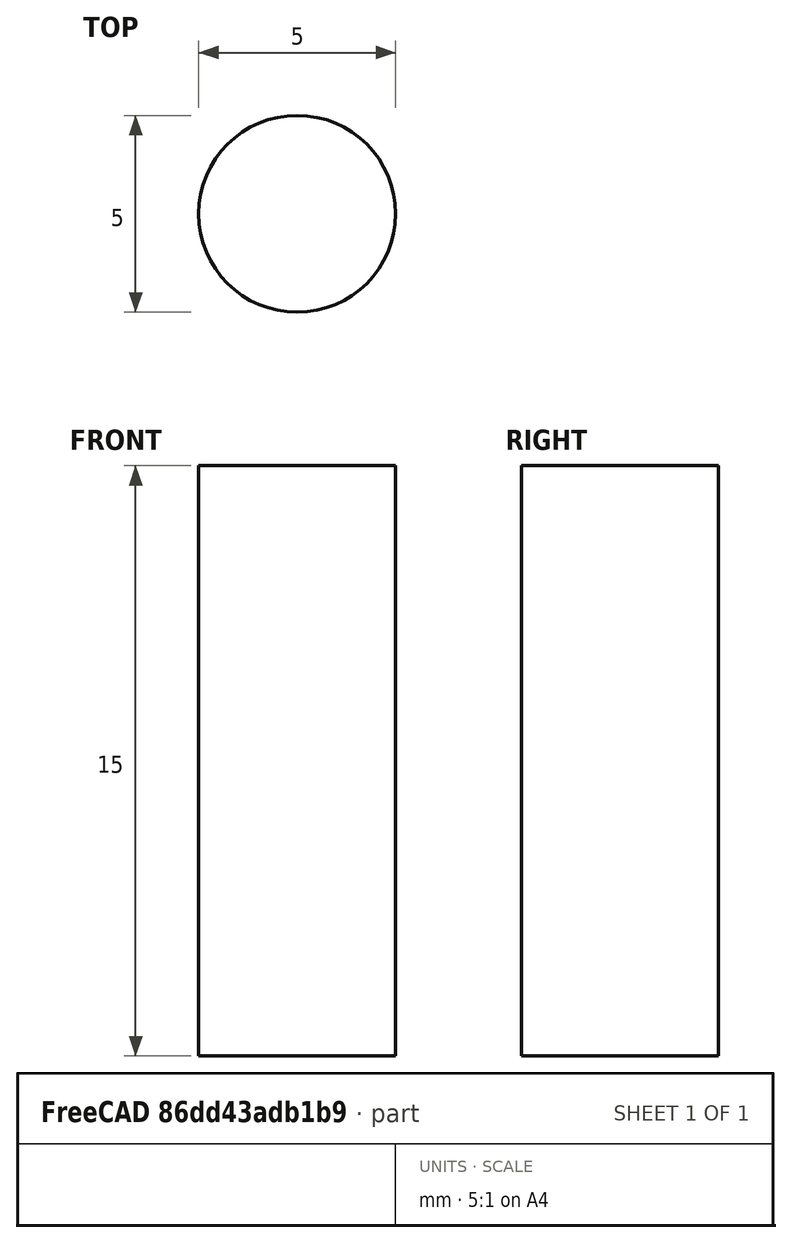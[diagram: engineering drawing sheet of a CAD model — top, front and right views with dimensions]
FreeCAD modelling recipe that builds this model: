
FCSTD DOCUMENT  (FreeCAD 1.0R39285 (Git))
Label: Box Pin
License: All rights reserved
LicenseURL: https://en.wikipedia.org/wiki/All_rights_reserved
objects: Sketcher::SketchObject×1, PartDesign::Pad×1, PartDesign::Body×1
note: 6 computed .brp shape members not serialized (recipe doc carries the construction recipe); baked Part::Feature solids carry a one-line shape summary decoded from their .brp

FEATURE [Sketcher::SketchObject] Sketch
  ArcFitTolerance = 1e-06
  AttachmentSupport = -> [XY_Plane]
  FullyConstrained = true
  MakeInternals = false
  MapMode = 5
  sketch-geometry (1):
    g0: Circle CenterX=0 CenterY=0 CenterZ=0 NormalX=0 NormalY=0 NormalZ=1 AngleXU=0 Radius=2.5
  constraints (2):
    c: Diameter(g0) = 5
    c: Coincident(g0,g-1)
FEATURE [PartDesign::Pad] Pad
  Direction = (0,0,1)
  Length = 15
  Length2 = 10
  Profile = -> Sketch
  ReferenceAxis = -> Sketch [N_Axis]
  Refine = true
  Suppressed = false
  Type = 0
FEATURE [PartDesign::Body] Body
  AllowCompound = false
  Group = -> [Sketch,Pad]
  Origin = -> Origin
  Tip = -> Pad
